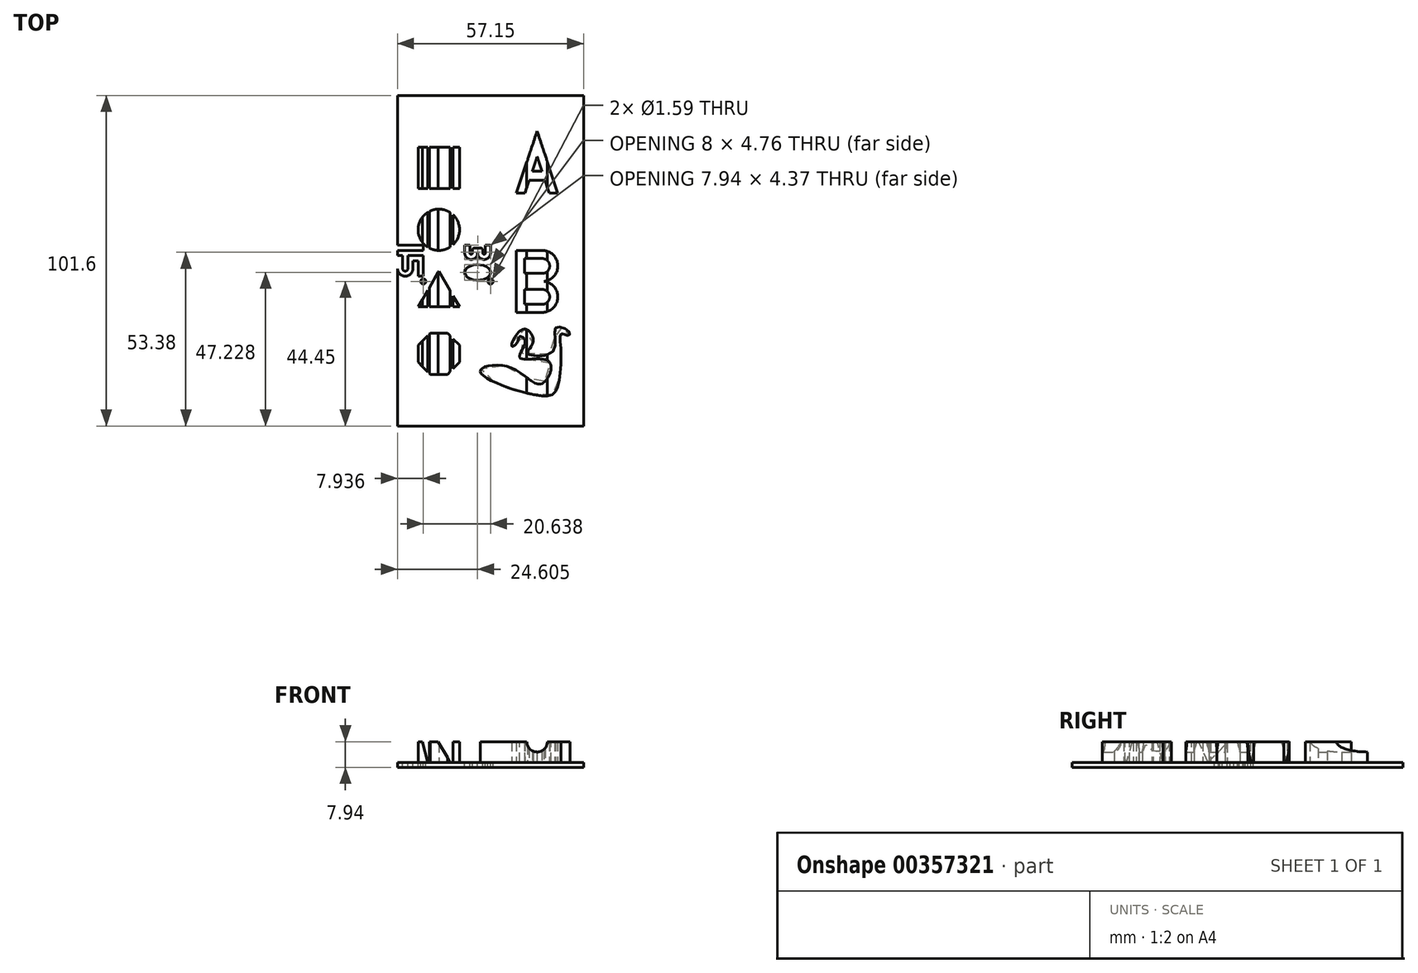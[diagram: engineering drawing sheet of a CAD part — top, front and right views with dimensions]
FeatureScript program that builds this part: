
annotation { "Feature Type Name" : "Feature", "Feature Type Description" : "" }
export const myFeature = defineFeature(function(context is Context, id is Id, definition is map)
    precondition{}
    {
        {
            var Q0;
            Q0=qCreatedBy(makeId("Top.planeOp"),FACE);
            var sketch = newSketch(context, id + "F0", { "sketchPlane" : qUnion([Q0])});
            skLineSegment(sketch, "E0.bottom", {"start": v(-42.88, 57.15) * mm, "end": v(14.27, 57.15) * mm});
            skLineSegment(sketch, "E0.top", {"start": v(-42.88, -44.45) * mm, "end": v(14.27, -44.45) * mm});
            skLineSegment(sketch, "E0.left", {"start": v(-42.88, 57.15) * mm, "end": v(-42.88, -44.45) * mm});
            skLineSegment(sketch, "E0.right", {"start": v(14.27, 57.15) * mm, "end": v(14.27, -44.45) * mm});
            skSolve(sketch);
        }
        {
            var Q0;
            Q0=makeQuery(id+"F0.imprint","IMPRINT",FACE,{"disambiguationData":[TD([[makeQuery(id+"F0.imprint","IMPRINT",EDGE,{"derivedFrom":sQuery(id+"F0.wireOp",EDGE,"E0.bottom")}),-1.0]])]});
            extrude(context, id + "F1", {"entities" : qUnion([Q0]), "depth" : 1.59 * mm});
        }
        {
            var Q0;
            Q0=makeQuery(id+"F1.opExtrude","CAP_FACE",FACE,{"disambiguationData":[OSD([sQuery(id+"F0.wireOp",EDGE,"E0.bottom"),sQuery(id+"F0.wireOp",EDGE,"E0.top"),sQuery(id+"F0.wireOp",EDGE,"E0.left"),sQuery(id+"F0.wireOp",EDGE,"E0.right")])],"isStart":false});
            var sketch = newSketch(context, id + "F2", { "sketchPlane" : qUnion([Q0])});
            skLineSegment(sketch, "E1.bottom", {"start": v(-36.53, 41.28) * mm, "end": v(-23.83, 41.28) * mm});
            skLineSegment(sketch, "E1.top", {"start": v(-36.53, 28.58) * mm, "end": v(-23.83, 28.58) * mm});
            skLineSegment(sketch, "E1.left", {"start": v(-36.53, 41.28) * mm, "end": v(-36.53, 28.58) * mm});
            skLineSegment(sketch, "E1.right", {"start": v(-23.83, 41.28) * mm, "end": v(-23.83, 28.58) * mm});
            skCircle(sketch, "E2", {"center": v(-30.18, 15.88) * mm, "radius": 6.35 * mm});
            skLineSegment(sketch, "E3", {"start": v(-36.53, -7.82) * mm, "end": v(-30.18, 3.18) * mm});
            skLineSegment(sketch, "E4", {"start": v(-30.18, 3.18) * mm, "end": v(-23.83, -7.82) * mm});
            skLineSegment(sketch, "E5", {"start": v(-23.83, -7.82) * mm, "end": v(-36.53, -7.82) * mm});
            skCircle(sketch, "E6.cCircle", {"center": v(-30.18, -22.22) * mm, "radius": 6.87 * mm, "construction": true});
            skLineSegment(sketch, "E6.0", {"start": v(-23.83, -19.6) * mm, "end": v(-23.83, -24.86) * mm});
            skLineSegment(sketch, "E6.1", {"start": v(-23.83, -24.86) * mm, "end": v(-27.55, -28.57) * mm});
            skLineSegment(sketch, "E6.2", {"start": v(-27.55, -28.57) * mm, "end": v(-32.81, -28.57) * mm});
            skLineSegment(sketch, "E6.3", {"start": v(-32.81, -28.57) * mm, "end": v(-36.53, -24.86) * mm});
            skLineSegment(sketch, "E6.4", {"start": v(-36.53, -24.86) * mm, "end": v(-36.53, -19.6) * mm});
            skLineSegment(sketch, "E6.5", {"start": v(-36.53, -19.6) * mm, "end": v(-32.81, -15.87) * mm});
            skLineSegment(sketch, "E6.6", {"start": v(-32.81, -15.87) * mm, "end": v(-27.55, -15.87) * mm});
            skLineSegment(sketch, "E6.7", {"start": v(-27.55, -15.87) * mm, "end": v(-23.83, -19.6) * mm});
            skLineSegment(sketch, "E7", {"start": v(-6.35, 27.17) * mm, "end": v(0, 46.22) * mm});
            skLineSegment(sketch, "E8", {"start": v(-6.35, 27.17) * mm, "end": v(-3.73, 27.17) * mm});
            skLineSegment(sketch, "E9", {"start": v(-3.73, 27.17) * mm, "end": v(-2.43, 31.04) * mm});
            skLineSegment(sketch, "E10", {"start": v(-2.43, 31.04) * mm, "end": v(0, 31.04) * mm});
            skLineSegment(sketch, "E11", {"start": v(0, 38.35) * mm, "end": v(-1.48, 33.9) * mm});
            skLineSegment(sketch, "E12", {"start": v(-1.48, 33.9) * mm, "end": v(0, 33.9) * mm});
            skLineSegment(sketch, "E13.MirrorCS", {"start": v(6.35, 27.17) * mm, "end": v(0, 46.22) * mm});
            skLineSegment(sketch, "E14.MirrorCS", {"start": v(0, 38.35) * mm, "end": v(1.48, 33.9) * mm});
            skLineSegment(sketch, "E15.MirrorCS", {"start": v(1.48, 33.9) * mm, "end": v(0, 33.9) * mm});
            skLineSegment(sketch, "E16.MirrorCS", {"start": v(2.43, 31.04) * mm, "end": v(0, 31.04) * mm});
            skLineSegment(sketch, "E17.MirrorCS", {"start": v(3.73, 27.17) * mm, "end": v(2.43, 31.04) * mm});
            skLineSegment(sketch, "E18.MirrorCS", {"start": v(6.35, 27.17) * mm, "end": v(3.73, 27.17) * mm});
            skLineSegment(sketch, "E19", {"start": v(-6.35, 9.52) * mm, "end": v(-6.35, -9.53) * mm});
            skLineSegment(sketch, "E20", {"start": v(-6.35, 9.52) * mm, "end": v(6.35, 9.53) * mm});
            skLineSegment(sketch, "E21", {"start": v(6.35, 9.53) * mm, "end": v(6.35, -9.53) * mm});
            skLineSegment(sketch, "E22", {"start": v(6.35, -9.53) * mm, "end": v(-6.35, -9.53) * mm});
            skArc(sketch, "E23.trimOffspring", {"start": v(2.11, 0) * mm, "mid": v(6.34, 5.02) * mm, "end": v(1.57, 9.53) * mm});
            skArc(sketch, "E24.trimOffspring", {"start": v(1.57, -9.52) * mm, "mid": v(6.34, -5.02) * mm, "end": v(2.11, 0) * mm});
            skLineSegment(sketch, "E25.bottom", {"start": v(-3.86, -2.46) * mm, "end": v(1.57, -2.46) * mm});
            skLineSegment(sketch, "E25.top", {"start": v(-3.86, -7.04) * mm, "end": v(1.57, -7.04) * mm});
            skLineSegment(sketch, "E25.left", {"start": v(-3.86, -2.46) * mm, "end": v(-3.86, -7.04) * mm});
            skArc(sketch, "E26", {"start": v(1.57, -7.04) * mm, "mid": v(3.86, -4.75) * mm, "end": v(1.57, -2.46) * mm});
            skLineSegment(sketch, "E27.MirrorCS", {"start": v(-3.86, 2.46) * mm, "end": v(1.57, 2.46) * mm});
            skLineSegment(sketch, "E28.MirrorCS", {"start": v(-3.86, 2.46) * mm, "end": v(-3.86, 7.04) * mm});
            skLineSegment(sketch, "E29.MirrorCS", {"start": v(-3.86, 7.04) * mm, "end": v(1.57, 7.04) * mm});
            skArc(sketch, "E30.MirrorCS", {"start": v(1.57, 7.04) * mm, "mid": v(3.86, 4.75) * mm, "end": v(1.57, 2.46) * mm});
            skFitSpline(sketch, "E31", {"points": [v(-6.06, -18.68) * mm, v(-5.23, -16.89) * mm, v(-3.7, -18.55) * mm, v(-5.3, -23.46) * mm, v(3.7, -24.7) * mm, v(1.41, -31.4) * mm, v(-8.27, -26.43) * mm, v(-17.48, -27.74) * mm, v(1.83, -35.21) * mm, v(6.04, -33) * mm, v(7.29, -21.31) * mm, v(7.57, -16.06) * mm, v(9.7, -16.61) * mm, v(9.78, -15.37) * mm, v(5.7, -14.33) * mm, v(4.94, -21.45) * mm, v(-2.95, -22.07) * mm, v(-1.22, -18.68) * mm, v(-4.26, -14.67) * mm, v(-7.79, -19.86) * mm, v(-6.06, -18.68) * mm]});
            skSolve(sketch);
        }
        {
            var Q0;
            Q0=makeQuery(id+"F2.imprint","IMPRINT",FACE,{"disambiguationData":[TD([[makeQuery(id+"F2.imprint","IMPRINT",EDGE,{"derivedFrom":sQuery(id+"F2.wireOp",EDGE,"E1.bottom")}),-1.0]])]});
            var Q1;
            Q1=makeQuery(id+"F2.imprint","IMPRINT",FACE,{"disambiguationData":[TD([[makeQuery(id+"F2.imprint","IMPRINT",EDGE,{"derivedFrom":sQuery(id+"F2.wireOp",EDGE,"E7")}),-1.0]])]});
            var Q2;
            {var subQ10=sQuery(id+"F2.wireOp",EDGE,"E19");Q2=makeQuery(id+"F2.imprint","IMPRINT",FACE,{"disambiguationData":[TD([[makeQuery(id+"F2.imprint","IMPRINT",EDGE,{"derivedFrom":subQ10}),1.0]])]});}
            var Q3;
            Q3=makeQuery(id+"F2.imprint","IMPRINT",FACE,{"disambiguationData":[TD([[makeQuery(id+"F2.imprint","IMPRINT",EDGE,{"derivedFrom":sQuery(id+"F2.wireOp",EDGE,"E2")}),1.0]])]});
            var Q4;
            Q4=makeQuery(id+"F2.imprint","IMPRINT",FACE,{"disambiguationData":[TD([[makeQuery(id+"F2.imprint","IMPRINT",EDGE,{"derivedFrom":sQuery(id+"F2.wireOp",EDGE,"E3")}),-1.0]])]});
            var Q5;
            Q5=makeQuery(id+"F2.imprint","IMPRINT",FACE,{"disambiguationData":[TD([[makeQuery(id+"F2.imprint","IMPRINT",EDGE,{"derivedFrom":sQuery(id+"F2.wireOp",EDGE,"E6.0")}),-1.0]])]});
            var Q6;
            Q6=makeQuery(id+"F2.imprint","IMPRINT",FACE,{"disambiguationData":[TD([[makeQuery(id+"F2.imprint","IMPRINT",EDGE,{"derivedFrom":sQuery(id+"F2.wireOp",EDGE,"E31")}),1.0]])]});
            extrude(context, id + "F3", {"entities" : qUnion([Q0, Q1, Q2, Q3, Q4, Q5, Q6]), "operationType" : NewBodyOperationType.ADD, "depth" : 6.35 * mm});
        }
        {
            var Q0;
            Q0=makeQuery(id+"F1.opExtrude","SWEPT_FACE",FACE,{"disambiguationData":[OSD([sQuery(id+"F0.wireOp",EDGE,"E0.top")])]});
            var sketch = newSketch(context, id + "F4", { "sketchPlane" : qUnion([Q0])});
            skLineSegment(sketch, "E32", {"start": v(-36.53, 0) * mm, "end": v(-36.53, 12.7) * mm});
            skLineSegment(sketch, "E33", {"start": v(-36.53, 12.7) * mm, "end": v(-33.13, 0) * mm});
            skLineSegment(sketch, "E34", {"start": v(-33.13, 0) * mm, "end": v(-36.53, 0) * mm});
            skLineSegment(sketch, "E35", {"start": v(-33.13, 0) * mm, "end": v(-33.13, 12.7) * mm});
            skLineSegment(sketch, "E36", {"start": v(-33.13, 12.7) * mm, "end": v(-25.8, 0) * mm});
            skLineSegment(sketch, "E37", {"start": v(-25.8, 0) * mm, "end": v(-33.13, 0) * mm});
            skLineSegment(sketch, "E38", {"start": v(-25.8, 0) * mm, "end": v(-25.8, 12.7) * mm});
            skLineSegment(sketch, "E39", {"start": v(-25.8, 12.7) * mm, "end": v(-36.53, 12.7) * mm});
            skSolve(sketch);
        }
        {
            var Q0;
            {var subQ1=sQuery(id+"F4.wireOp",EDGE,"E33");var subQ3=makeQuery(id+"F1.opExtrude","CAP_EDGE",EDGE,{"disambiguationData":[OSD([sQuery(id+"F0.wireOp",EDGE,"E0.top")])],"isStart":false});var subQ4=makeQuery(id+"F4.imprint","INTERSECT",VERTEX,{"derivedFrom":[subQ3,subQ1]});Q0=makeQuery(id+"F4.imprint","IMPRINT",FACE,{"disambiguationData":[TD([[makeQuery(id+"F4.imprint","IMPRINT",EDGE,{"disambiguationData":[TD([[subQ4,-1.0]])],"derivedFrom":subQ3}),1.0]])]});}
            var Q1;
            {var subQ0=sQuery(id+"F4.wireOp",EDGE,"E39");var subQ5=sQuery(id+"F4.wireOp",EDGE,"E38");var subQ6=makeQuery(id+"F4.imprint","INTERSECT",VERTEX,{"derivedFrom":[subQ5,subQ0]});Q1=makeQuery(id+"F4.imprint","IMPRINT",FACE,{"disambiguationData":[TD([[makeQuery(id+"F4.imprint","IMPRINT",EDGE,{"disambiguationData":[TD([[subQ6,1.0]])],"derivedFrom":subQ5}),1.0]])]});}
            extrude(context, id + "F5", {"entities" : qUnion([Q0, Q1]), "operationType" : NewBodyOperationType.REMOVE, "endBound" : BoundingType.THROUGH_ALL, "oppositeDirection" : true, "depth" : 101.6 * mm});
        }
        {
            var Q0;
            {var subQ0=makeQuery(id+"F3.opExtrude","SWEPT_FACE",FACE,{"disambiguationData":[OSD([sQuery(id+"F2.wireOp",EDGE,"E6.3")])]});var subQ1=sQuery(id+"F0.wireOp",EDGE,"E0.bottom");var subQ2=makeQuery(id+"F1.opExtrude","SWEPT_FACE",FACE,{"disambiguationData":[OSD([subQ1])]});var subQ3=makeQuery(id+"F3.opExtrude","SWEPT_FACE",FACE,{"disambiguationData":[OSD([sQuery(id+"F2.wireOp",EDGE,"E3")])]});var subQ4=makeQuery(id+"F3.opExtrude","SWEPT_FACE",FACE,{"disambiguationData":[OSD([sQuery(id+"F2.wireOp",EDGE,"E2")])]});var subQ5=makeQuery(id+"F3.opExtrude","SWEPT_FACE",FACE,{"disambiguationData":[OSD([sQuery(id+"F2.wireOp",EDGE,"E1.left")])]});var subQ6=makeQuery(id+"F3.opExtrude","SWEPT_FACE",FACE,{"disambiguationData":[OSD([sQuery(id+"F2.wireOp",EDGE,"E5")])]});var subQ7=sQuery(id+"F0.wireOp",EDGE,"E0.top");var subQ8=makeQuery(id+"F1.opExtrude","SWEPT_FACE",FACE,{"disambiguationData":[OSD([subQ7])]});var subQ9=makeQuery(id+"F3.opExtrude","SWEPT_FACE",FACE,{"disambiguationData":[OSD([sQuery(id+"F2.wireOp",EDGE,"E1.bottom")])]});var subQ10=sQuery(id+"F0.wireOp",EDGE,"E0.left");var subQ11=makeQuery(id+"F1.opExtrude","SWEPT_FACE",FACE,{"disambiguationData":[OSD([subQ10])]});var subQ12=makeQuery(id+"F3.opExtrude","SWEPT_FACE",FACE,{"disambiguationData":[OSD([sQuery(id+"F2.wireOp",EDGE,"E1.top")])]});var subQ13=makeQuery(id+"F3.opExtrude","SWEPT_FACE",FACE,{"disambiguationData":[OSD([sQuery(id+"F2.wireOp",EDGE,"E6.4")])]});var subQ14=makeQuery(id+"F3.opExtrude","SWEPT_FACE",FACE,{"disambiguationData":[OSD([sQuery(id+"F2.wireOp",EDGE,"E6.5")])]});var subQ15=sQuery(id+"F0.wireOp",EDGE,"E0.right");Q0=makeQuery(id+"F5.boolean.opBoolean","SPLIT",FACE,{"disambiguationData":[TD([subQ2,subQ8,subQ11,subQ9,subQ12,subQ5,subQ4,subQ3,subQ6,subQ0,subQ13,subQ14,makeQuery(id+"F5.opExtrude","SWEPT_FACE",FACE,{"disambiguationData":[OSD([sQuery(id+"F4.wireOp",EDGE,"E33")])]})])],"derivedFrom":makeQuery(id+"F3.boolean.opBoolean","SPLIT",FACE,{"disambiguationData":[TD([subQ2])],"derivedFrom":makeQuery(id+"F1.opExtrude","CAP_FACE",FACE,{"disambiguationData":[OSD([subQ1,subQ7,subQ10,subQ15])],"isStart":false})})});}
            var sketch = newSketch(context, id + "F6", { "sketchPlane" : qUnion([Q0])});
            skLineSegment(sketch, "E40", {"start": v(-42.88, 11.11) * mm, "end": v(-34.94, 11.11) * mm});
            skPoint(sketch, "E40.endSnap0", {"position": v(-34.94, 4.97) * mm});
            skLineSegment(sketch, "E41", {"start": v(-42.88, 11.11) * mm, "end": v(-42.88, 9.53) * mm});
            skLineSegment(sketch, "E42", {"start": v(-42.88, 9.53) * mm, "end": v(-34.94, 9.53) * mm});
            skLineSegment(sketch, "E43", {"start": v(-34.94, 11.11) * mm, "end": v(-34.94, 9.53) * mm});
            skLineSegment(sketch, "E44", {"start": v(-42.88, 7.94) * mm, "end": v(-42.88, 3.97) * mm});
            skLineSegment(sketch, "E45", {"start": v(-36.53, 1.59) * mm, "end": v(-34.94, 1.59) * mm});
            skLineSegment(sketch, "E46", {"start": v(-34.94, 1.59) * mm, "end": v(-34.94, 7.94) * mm});
            skLineSegment(sketch, "E47", {"start": v(-34.94, 7.94) * mm, "end": v(-39.7, 7.94) * mm});
            skArc(sketch, "E48", {"start": v(-42.88, 3.97) * mm, "mid": v(-40.5, 1.59) * mm, "end": v(-38.12, 3.97) * mm});
            skArc(sketch, "E49", {"start": v(-41.31, 3.97) * mm, "mid": v(-40.5, 3.16) * mm, "end": v(-39.7, 3.97) * mm});
            skLineSegment(sketch, "E50", {"start": v(-36.53, 1.59) * mm, "end": v(-36.53, 6.35) * mm});
            skLineSegment(sketch, "E51", {"start": v(-36.53, 6.35) * mm, "end": v(-38.12, 6.35) * mm});
            skLineSegment(sketch, "E52", {"start": v(-38.12, 6.35) * mm, "end": v(-38.12, 3.97) * mm});
            skLineSegment(sketch, "E53", {"start": v(-41.31, 7.94) * mm, "end": v(-41.31, 3.97) * mm});
            skLineSegment(sketch, "E54", {"start": v(-39.7, 3.97) * mm, "end": v(-39.7, 7.94) * mm});
            skLineSegment(sketch, "E55.trimOffspring", {"start": v(-41.31, 7.94) * mm, "end": v(-42.88, 7.94) * mm});
            skCircle(sketch, "E56", {"center": v(-34.94, 0) * mm, "radius": 0.8 * mm});
            skCircle(sketch, "E57", {"center": v(-14.3, 0) * mm, "radius": 0.8 * mm});
            skArc(sketch, "E58", {"start": v(-18.28, 8.73) * mm, "mid": v(-16.3, 6.75) * mm, "end": v(-14.3, 8.73) * mm});
            skArc(sketch, "E59", {"start": v(-22.24, 8.73) * mm, "mid": v(-20.26, 6.75) * mm, "end": v(-18.28, 8.73) * mm});
            skLineSegment(sketch, "E60", {"start": v(-14.3, 8.73) * mm, "end": v(-14.3, 11.11) * mm});
            skLineSegment(sketch, "E61", {"start": v(-14.3, 11.11) * mm, "end": v(-15.9, 11.11) * mm});
            skLineSegment(sketch, "E62", {"start": v(-22.24, 8.73) * mm, "end": v(-22.24, 11.11) * mm});
            skLineSegment(sketch, "E63", {"start": v(-22.24, 11.11) * mm, "end": v(-20.66, 11.11) * mm});
            skLineSegment(sketch, "E64", {"start": v(-20.66, 11.11) * mm, "end": v(-20.66, 8.73) * mm});
            skLineSegment(sketch, "E65", {"start": v(-15.9, 11.11) * mm, "end": v(-15.9, 8.73) * mm});
            skArc(sketch, "E66", {"start": v(-16.69, 8.73) * mm, "mid": v(-16.3, 8.33) * mm, "end": v(-15.9, 8.73) * mm});
            skArc(sketch, "E67", {"start": v(-20.66, 8.73) * mm, "mid": v(-20.26, 8.33) * mm, "end": v(-19.86, 8.73) * mm});
            skLineSegment(sketch, "E68", {"start": v(-19.86, 8.73) * mm, "end": v(-19.86, 9.53) * mm});
            skLineSegment(sketch, "E69", {"start": v(-19.07, 10.32) * mm, "end": v(-17.48, 10.32) * mm});
            skLineSegment(sketch, "E70", {"start": v(-16.69, 8.73) * mm, "end": v(-16.69, 9.53) * mm});
            skArc(sketch, "E71", {"start": v(-16.69, 9.53) * mm, "mid": v(-16.92, 10.09) * mm, "end": v(-17.48, 10.32) * mm});
            skArc(sketch, "E72", {"start": v(-19.07, 10.32) * mm, "mid": v(-19.63, 10.09) * mm, "end": v(-19.86, 9.53) * mm});
            skEllipse(sketch, "E73", {"center": v(-18.28, 2.78) * mm, "majorRadius": 4 * mm, "minorRadius": 2.38 * mm, "majorAxis": v(1, 0)});
            skSolve(sketch);
        }
        {
            var Q0;
            Q0=makeQuery(id+"F6.imprint","IMPRINT",FACE,{"disambiguationData":[TD([[makeQuery(id+"F6.imprint","IMPRINT",EDGE,{"derivedFrom":sQuery(id+"F6.wireOp",EDGE,"E58")}),1.0]])]});
            var Q1;
            Q1=makeQuery(id+"F6.imprint","IMPRINT",FACE,{"disambiguationData":[TD([[makeQuery(id+"F6.imprint","IMPRINT",EDGE,{"derivedFrom":sQuery(id+"F6.wireOp",EDGE,"E73")}),1.0]])]});
            var Q2;
            Q2=makeQuery(id+"F6.imprint","IMPRINT",FACE,{"disambiguationData":[TD([[makeQuery(id+"F6.imprint","IMPRINT",EDGE,{"derivedFrom":sQuery(id+"F6.wireOp",EDGE,"E57")}),1.0]])]});
            var Q3;
            Q3=makeQuery(id+"F6.imprint","IMPRINT",FACE,{"disambiguationData":[TD([[makeQuery(id+"F6.imprint","IMPRINT",EDGE,{"derivedFrom":sQuery(id+"F6.wireOp",EDGE,"E40")}),-1.0]])]});
            var Q4;
            Q4=makeQuery(id+"F6.imprint","IMPRINT",FACE,{"disambiguationData":[TD([[makeQuery(id+"F6.imprint","IMPRINT",EDGE,{"derivedFrom":sQuery(id+"F6.wireOp",EDGE,"E44")}),1.0]])]});
            var Q5;
            Q5=makeQuery(id+"F6.imprint","IMPRINT",FACE,{"disambiguationData":[TD([[makeQuery(id+"F6.imprint","IMPRINT",EDGE,{"derivedFrom":sQuery(id+"F6.wireOp",EDGE,"E56")}),1.0]])]});
            var Q6;
            {var subQ0=sQuery(id+"F0.wireOp",EDGE,"E0.bottom");var subQ1=sQuery(id+"F0.wireOp",EDGE,"E0.right");var subQ2=sQuery(id+"F0.wireOp",EDGE,"E0.top");Q6=makeQuery(id+"F5.boolean.opBoolean","SPLIT",FACE,{"disambiguationData":[TD([makeQuery(id+"F1.opExtrude","SWEPT_FACE",FACE,{"disambiguationData":[OSD([subQ1])]})])],"derivedFrom":makeQuery(id+"F1.opExtrude","CAP_FACE",FACE,{"disambiguationData":[OSD([subQ0,subQ2,sQuery(id+"F0.wireOp",EDGE,"E0.left"),subQ1])],"isStart":true})});}
            extrude(context, id + "F7", {"entities" : qUnion([Q0, Q1, Q2, Q3, Q4, Q5]), "operationType" : NewBodyOperationType.REMOVE, "endBound" : BoundingType.UP_TO_SURFACE, "oppositeDirection" : true, "endBoundEntityFace" : qUnion([Q6]), "depth" : 25.4 * mm});
        }
        {
            var Q0;
            {var subQ0=sQuery(id+"F0.wireOp",EDGE,"E0.right");var subQ3=sQuery(id+"F0.wireOp",EDGE,"E0.bottom");Q0=makeQuery(id+"F5.boolean.opBoolean","SPLIT",FACE,{"disambiguationData":[TD([makeQuery(id+"F1.opExtrude","SWEPT_FACE",FACE,{"disambiguationData":[OSD([subQ0])]})])],"derivedFrom":makeQuery(id+"F1.opExtrude","SWEPT_FACE",FACE,{"disambiguationData":[OSD([subQ3])]})});}
            var sketch = newSketch(context, id + "F8", { "sketchPlane" : qUnion([Q0])});
            skCircle(sketch, "E74", {"center": v(0, 7.94) * mm, "radius": 3.18 * mm});
            skLineSegment(sketch, "E75", {"start": v(-3.18, 7.94) * mm, "end": v(3.18, 7.94) * mm});
            skSolve(sketch);
        }
        {
            var Q0;
            {var subQ0=sQuery(id+"F8.wireOp",EDGE,"E75");Q0=makeQuery(id+"F8.imprint","IMPRINT",FACE,{"disambiguationData":[TD([[makeQuery(id+"F8.imprint","IMPRINT",EDGE,{"derivedFrom":subQ0}),-1.0]])]});}
            var Q1;
            {var subQ0=sQuery(id+"F0.wireOp",EDGE,"E0.right");var subQ2=sQuery(id+"F0.wireOp",EDGE,"E0.top");Q1=makeQuery(id+"F5.boolean.opBoolean","SPLIT",FACE,{"disambiguationData":[TD([makeQuery(id+"F1.opExtrude","SWEPT_FACE",FACE,{"disambiguationData":[OSD([subQ0])]})])],"derivedFrom":makeQuery(id+"F1.opExtrude","SWEPT_FACE",FACE,{"disambiguationData":[OSD([subQ2])]})});}
            extrude(context, id + "F9", {"entities" : qUnion([Q0]), "operationType" : NewBodyOperationType.REMOVE, "endBound" : BoundingType.THROUGH_ALL, "oppositeDirection" : true, "endBoundEntityFace" : qUnion([Q1]), "depth" : 25.4 * mm});
        }
    });
